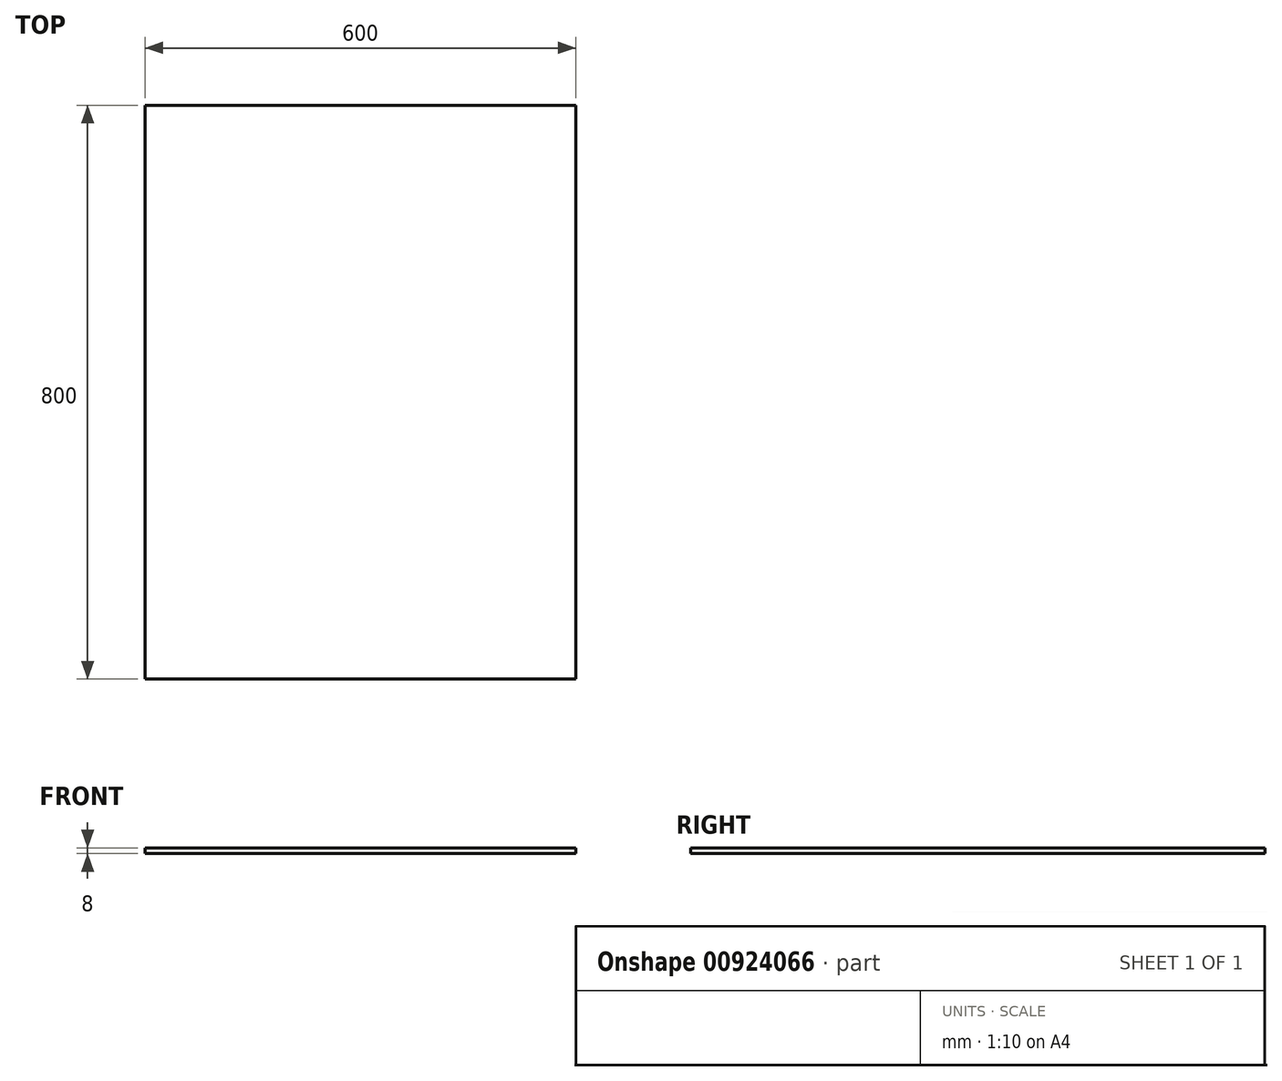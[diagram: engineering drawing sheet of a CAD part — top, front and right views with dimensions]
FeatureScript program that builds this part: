
annotation { "Feature Type Name" : "Feature", "Feature Type Description" : "" }
export const myFeature = defineFeature(function(context is Context, id is Id, definition is map)
    precondition{}
    {
        {
            var Q0;
            Q0=qCreatedBy(makeId("Top.planeOp"),FACE);
            var sketch = newSketch(context, id + "F0", { "sketchPlane" : qUnion([Q0])});
            skLineSegment(sketch, "E0.bottom", {"start": v(-304.09, 403.5) * mm, "end": v(295.91, 403.5) * mm});
            skLineSegment(sketch, "E0.top", {"start": v(-304.09, -396.5) * mm, "end": v(295.91, -396.5) * mm});
            skLineSegment(sketch, "E0.left", {"start": v(-304.09, 403.5) * mm, "end": v(-304.09, -396.5) * mm});
            skLineSegment(sketch, "E0.right", {"start": v(295.91, 403.5) * mm, "end": v(295.91, -396.5) * mm});
            skSolve(sketch);
        }
        {
            var Q0;
            Q0=makeQuery(id+"F0.imprint","IMPRINT",FACE,{"disambiguationData":[TD([[makeQuery(id+"F0.imprint","IMPRINT",EDGE,{"derivedFrom":sQuery(id+"F0.wireOp",EDGE,"E0.bottom")}),-1.0]])]});
            extrude(context, id + "F1", {"entities" : qUnion([Q0]), "depth" : 8 * mm, "offsetDistance" : 25 * mm});
        }
    });
